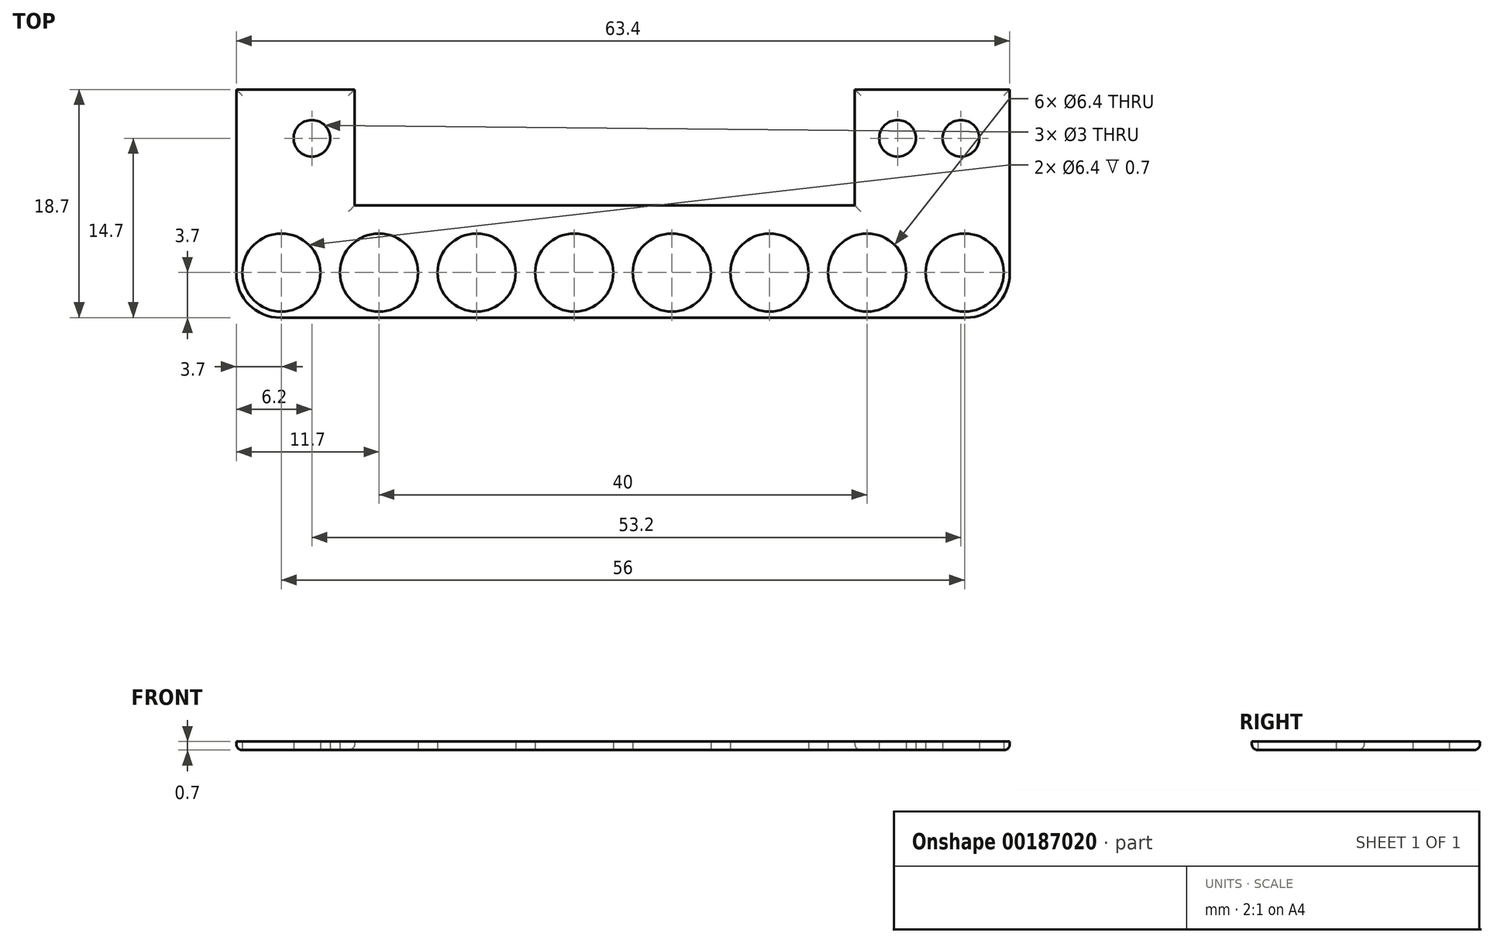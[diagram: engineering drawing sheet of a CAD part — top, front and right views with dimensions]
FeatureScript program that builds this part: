
annotation { "Feature Type Name" : "Feature", "Feature Type Description" : "" }
export const myFeature = defineFeature(function(context is Context, id is Id, definition is map)
    precondition{}
    {
        {
            var Q0;
            Q0=qCreatedBy(makeId("Top.planeOp"),FACE);
            var sketch = newSketch(context, id + "F0", { "sketchPlane" : qUnion([Q0])});
            skLineSegment(sketch, "E0", {"start": v(-31.7, 18.7) * mm, "end": v(-22, 18.7) * mm});
            skLineSegment(sketch, "E1", {"start": v(-22, 18.7) * mm, "end": v(-22, 9.2) * mm});
            skLineSegment(sketch, "E2", {"start": v(-22, 9.2) * mm, "end": v(19, 9.2) * mm});
            skLineSegment(sketch, "E3", {"start": v(19, 9.2) * mm, "end": v(19, 18.7) * mm});
            skLineSegment(sketch, "E4", {"start": v(19, 18.7) * mm, "end": v(31.7, 18.7) * mm});
            skLineSegment(sketch, "E5", {"start": v(31.7, 18.7) * mm, "end": v(31.7, 0) * mm});
            skLineSegment(sketch, "E6", {"start": v(31.7, 0) * mm, "end": v(-31.7, 0) * mm});
            skLineSegment(sketch, "E7", {"start": v(-31.7, 0) * mm, "end": v(-31.7, 18.7) * mm});
            skCircle(sketch, "E8", {"center": v(-25.5, 14.7) * mm, "radius": 1.5 * mm});
            skCircle(sketch, "E9", {"center": v(22.5, 14.7) * mm, "radius": 1.5 * mm});
            skCircle(sketch, "E10", {"center": v(-28, 3.7) * mm, "radius": 3.2 * mm});
            skCircle(sketch, "E11", {"center": v(4, 3.7) * mm, "radius": 3.2 * mm});
            skCircle(sketch, "E12", {"center": v(-12, 3.7) * mm, "radius": 3.2 * mm});
            skCircle(sketch, "E13", {"center": v(-4, 3.7) * mm, "radius": 3.2 * mm});
            skLineSegment(sketch, "E14.top", {"start": v(-10.35, 0) * mm, "end": v(-18.35, 0) * mm});
            skCircle(sketch, "E15", {"center": v(-20, 3.7) * mm, "radius": 3.2 * mm});
            skCircle(sketch, "E16", {"center": v(12, 3.7) * mm, "radius": 3.2 * mm});
            skCircle(sketch, "E17", {"center": v(20, 3.7) * mm, "radius": 3.2 * mm});
            skCircle(sketch, "E18", {"center": v(28, 3.7) * mm, "radius": 3.2 * mm});
            skCircle(sketch, "E19", {"center": v(27.7, 14.7) * mm, "radius": 1.5 * mm});
            skSolve(sketch);
        }
        {
            var Q0;
            Q0=makeQuery(id+"F0.imprint","IMPRINT",FACE,{"disambiguationData":[TD([[makeQuery(id+"F0.imprint","IMPRINT",EDGE,{"derivedFrom":sQuery(id+"F0.wireOp",EDGE,"E0")}),-1.0]])]});
            extrude(context, id + "F1", {"entities" : qUnion([Q0]), "depth" : 0.7 * mm});
        }
        {
            var Q0;
            Q0=makeQuery(id+"F1.opExtrude","CAP_EDGE",EDGE,{"disambiguationData":[OSD([sQuery(id+"F0.wireOp",EDGE,"E7")])],"isStart":true});
            var Q1;
            Q1=makeQuery(id+"F1.opExtrude","CAP_EDGE",EDGE,{"disambiguationData":[OSD([sQuery(id+"F0.wireOp",EDGE,"E6"),sQuery(id+"F0.wireOp",EDGE,"E14.top")])],"isStart":true});
            var Q2;
            Q2=makeQuery(id+"F1.opExtrude","CAP_EDGE",EDGE,{"disambiguationData":[OSD([sQuery(id+"F0.wireOp",EDGE,"E5")])],"isStart":true});
            var Q3;
            Q3=makeQuery(id+"F1.opExtrude","CAP_EDGE",EDGE,{"disambiguationData":[OSD([sQuery(id+"F0.wireOp",EDGE,"E4")])],"isStart":true});
            var Q4;
            Q4=makeQuery(id+"F1.opExtrude","CAP_EDGE",EDGE,{"disambiguationData":[OSD([sQuery(id+"F0.wireOp",EDGE,"E3")])],"isStart":true});
            var Q5;
            Q5=makeQuery(id+"F1.opExtrude","CAP_EDGE",EDGE,{"disambiguationData":[OSD([sQuery(id+"F0.wireOp",EDGE,"E2")])],"isStart":true});
            var Q6;
            Q6=makeQuery(id+"F1.opExtrude","CAP_EDGE",EDGE,{"disambiguationData":[OSD([sQuery(id+"F0.wireOp",EDGE,"E1")])],"isStart":true});
            var Q7;
            Q7=makeQuery(id+"F1.opExtrude","CAP_EDGE",EDGE,{"disambiguationData":[OSD([sQuery(id+"F0.wireOp",EDGE,"E0")])],"isStart":true});
            fillet(context, id + "F2", {"entities" : qUnion([Q0, Q1, Q2, Q3, Q4, Q5, Q6, Q7]), "radius" : 0.5 * mm, "tangentPropagation" : true, "allowEdgeOverflow" : false});
        }
        {
            var Q0;
            Q0=makeQuery(id+"F1.opExtrude","SWEPT_EDGE",EDGE,{"disambiguationData":[OSD([sQuery(id+"F0.wireOp",EDGE,"E6"),sQuery(id+"F0.wireOp",EDGE,"E7")])]});
            var Q1;
            Q1=makeQuery(id+"F2.opFillet","BLEND_EDGE",EDGE,{"blendedFrom":[makeQuery(id+"F1.opExtrude","CAP_EDGE",EDGE,{"disambiguationData":[OSD([sQuery(id+"F0.wireOp",EDGE,"E6"),sQuery(id+"F0.wireOp",EDGE,"E14.top")])],"isStart":true}),makeQuery(id+"F1.opExtrude","CAP_EDGE",EDGE,{"disambiguationData":[OSD([sQuery(id+"F0.wireOp",EDGE,"E7")])],"isStart":true})],"blendedInto":[]});
            var Q2;
            Q2=makeQuery(id+"F1.opExtrude","SWEPT_EDGE",EDGE,{"disambiguationData":[OSD([sQuery(id+"F0.wireOp",EDGE,"E5"),sQuery(id+"F0.wireOp",EDGE,"E6")])]});
            var Q3;
            Q3=makeQuery(id+"F2.opFillet","BLEND_EDGE",EDGE,{"blendedFrom":[makeQuery(id+"F1.opExtrude","CAP_EDGE",EDGE,{"disambiguationData":[OSD([sQuery(id+"F0.wireOp",EDGE,"E5")])],"isStart":true}),makeQuery(id+"F1.opExtrude","CAP_EDGE",EDGE,{"disambiguationData":[OSD([sQuery(id+"F0.wireOp",EDGE,"E6"),sQuery(id+"F0.wireOp",EDGE,"E14.top")])],"isStart":true})],"blendedInto":[]});
            fillet(context, id + "F3", {"entities" : qUnion([Q0, Q1, Q2, Q3]), "radius" : 3.6 * mm, "tangentPropagation" : true, "allowEdgeOverflow" : false});
        }
    });
